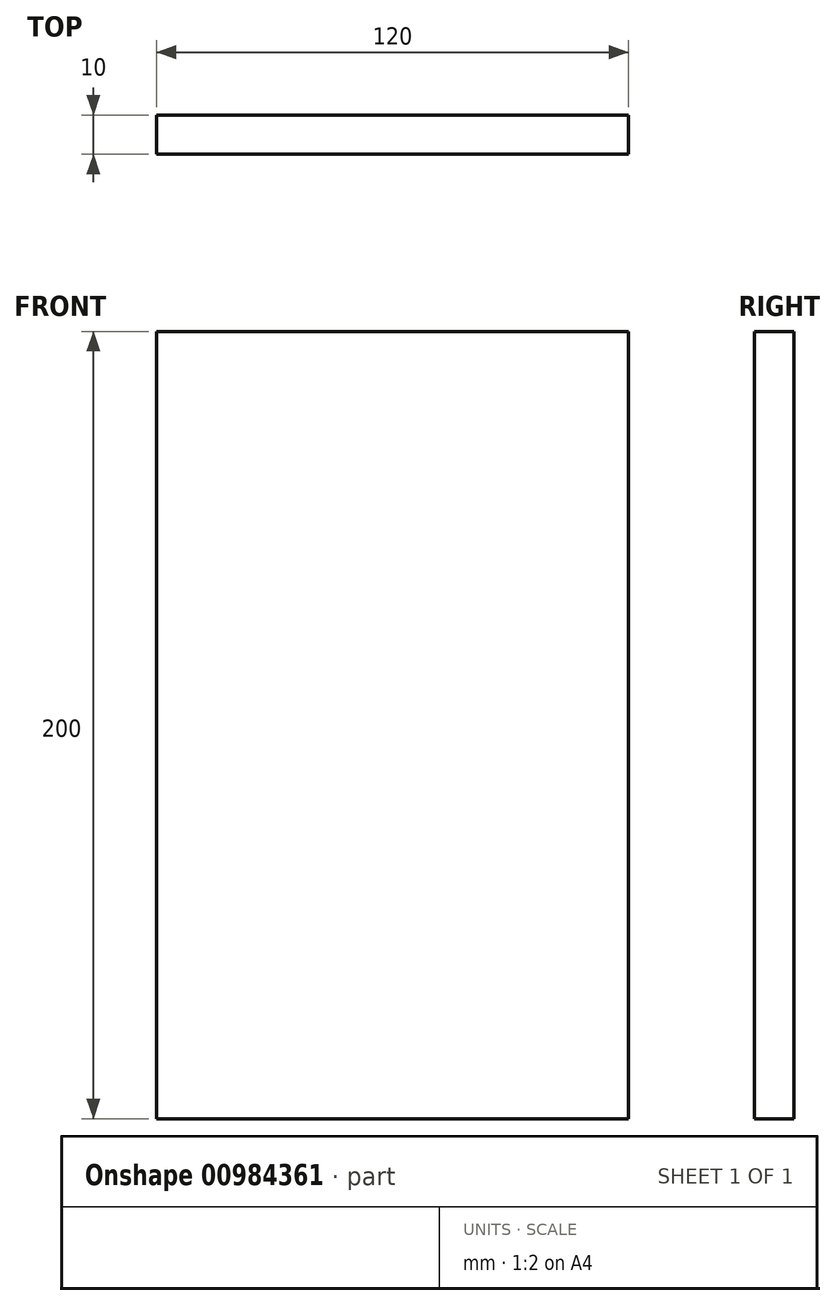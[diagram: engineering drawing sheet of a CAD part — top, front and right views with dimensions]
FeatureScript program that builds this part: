
annotation { "Feature Type Name" : "Feature", "Feature Type Description" : "" }
export const myFeature = defineFeature(function(context is Context, id is Id, definition is map)
    precondition{}
    {
        {
            var Q0;
            Q0=qCreatedBy(makeId("Front.planeOp"),FACE);
            var sketch = newSketch(context, id + "F0", { "sketchPlane" : qUnion([Q0])});
            skLineSegment(sketch, "E0.bottom", {"start": v(60, -100) * mm, "end": v(-60, -100) * mm});
            skLineSegment(sketch, "E0.top", {"start": v(60, 100) * mm, "end": v(-60, 100) * mm});
            skLineSegment(sketch, "E0.left", {"start": v(60, -100) * mm, "end": v(60, 100) * mm});
            skLineSegment(sketch, "E0.right", {"start": v(-60, -100) * mm, "end": v(-60, 100) * mm});
            skPoint(sketch, "E0.middle", {"position": v(0, 0) * mm});
            skSolve(sketch);
        }
        {
            var Q0;
            Q0=makeQuery(id+"F0.imprint","IMPRINT",FACE,{"disambiguationData":[TD([[makeQuery(id+"F0.imprint","IMPRINT",EDGE,{"derivedFrom":sQuery(id+"F0.wireOp",EDGE,"E0.bottom")}),-1.0]])]});
            extrude(context, id + "F1", {"entities" : qUnion([Q0]), "depth" : 10 * mm, "offsetDistance" : 25 * mm});
        }
    });
